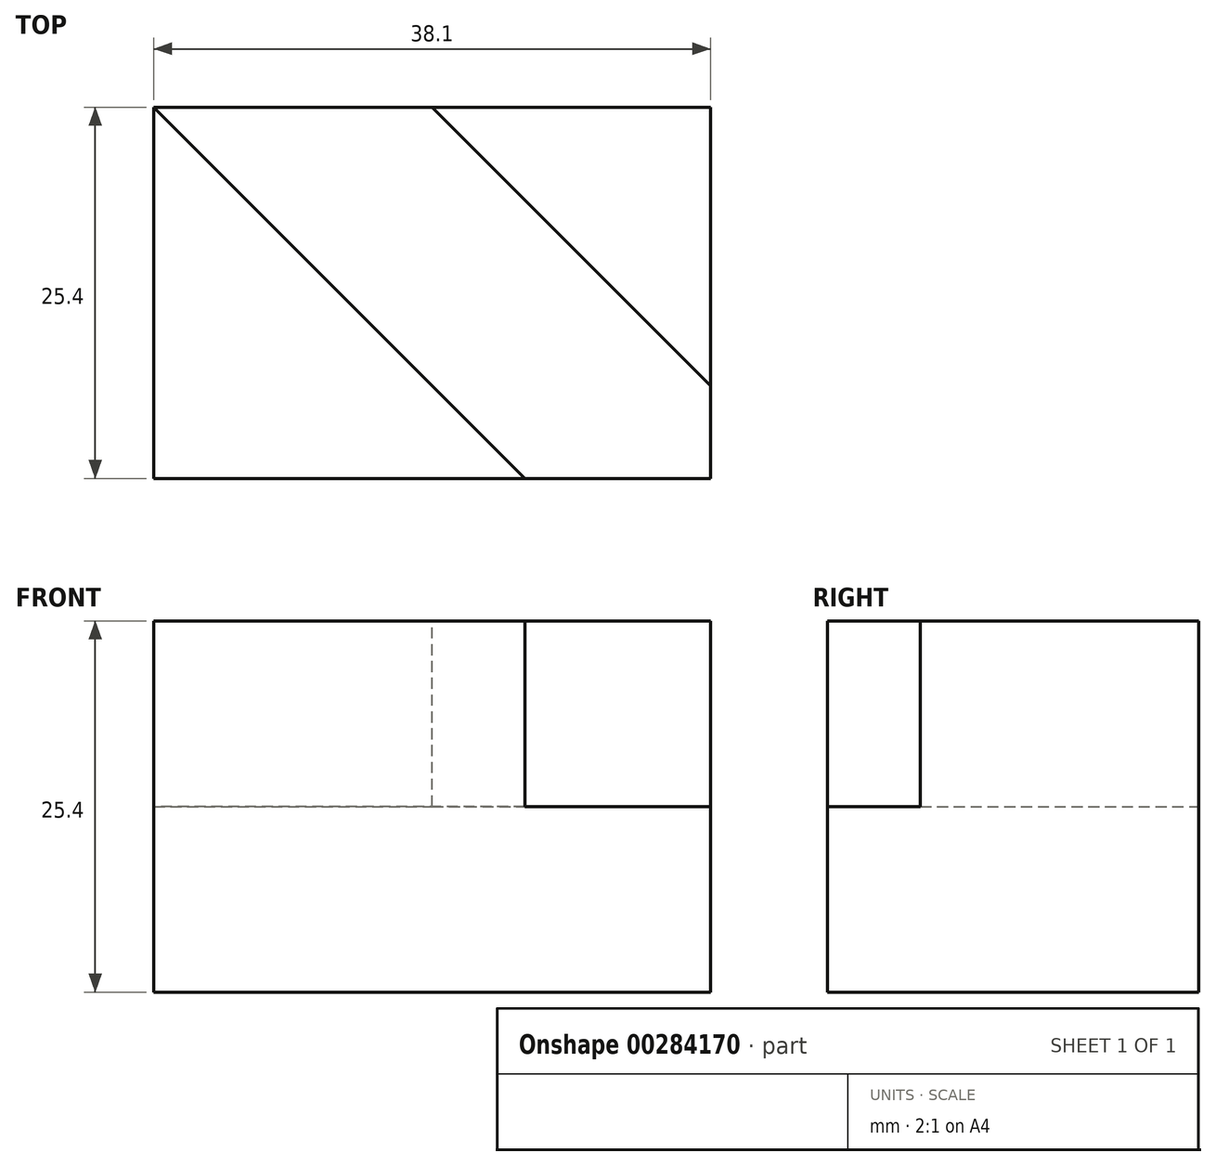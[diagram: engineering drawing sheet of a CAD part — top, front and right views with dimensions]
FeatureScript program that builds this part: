
annotation { "Feature Type Name" : "Feature", "Feature Type Description" : "" }
export const myFeature = defineFeature(function(context is Context, id is Id, definition is map)
    precondition{}
    {
        {
            var Q0;
            Q0=qCreatedBy(makeId("Front.planeOp"),FACE);
            var sketch = newSketch(context, id + "F0", { "sketchPlane" : qUnion([Q0])});
            skLineSegment(sketch, "E0.bottom", {"start": v(0, -25.4) * mm, "end": v(38.1, -25.4) * mm});
            skLineSegment(sketch, "E0.top", {"start": v(0, 0) * mm, "end": v(38.1, 0) * mm});
            skLineSegment(sketch, "E0.left", {"start": v(0, -25.4) * mm, "end": v(0, 0) * mm});
            skLineSegment(sketch, "E0.right", {"start": v(38.1, -25.4) * mm, "end": v(38.1, 0) * mm});
            skSolve(sketch);
        }
        {
            var Q0;
            Q0=makeQuery(id+"F0.imprint","IMPRINT",FACE,{"disambiguationData":[TD([[makeQuery(id+"F0.imprint","IMPRINT",EDGE,{"derivedFrom":sQuery(id+"F0.wireOp",EDGE,"E0.bottom")}),1.0]])]});
            extrude(context, id + "F1", {"entities" : qUnion([Q0]), "oppositeDirection" : true, "depth" : 25.4 * mm});
        }
        {
            var Q0;
            Q0=qCreatedBy(makeId("Top.planeOp"),FACE);
            var sketch = newSketch(context, id + "F2", { "sketchPlane" : qUnion([Q0])});
            skLineSegment(sketch, "E1", {"start": v(25.4, 0) * mm, "end": v(0, 25.4) * mm});
            skLineSegment(sketch, "E2", {"start": v(0, 25.4) * mm, "end": v(19.05, 25.4) * mm});
            skLineSegment(sketch, "E3", {"start": v(19.05, 25.4) * mm, "end": v(38.1, 6.35) * mm});
            skLineSegment(sketch, "E4", {"start": v(38.1, 6.35) * mm, "end": v(38.1, 0) * mm});
            skLineSegment(sketch, "E5", {"start": v(38.1, 0) * mm, "end": v(25.4, 0) * mm});
            skSolve(sketch);
        }
        {
            var Q0;
            Q0 = qSketchRegion(id + "F2", true);
            extrude(context, id + "F3", {"entities" : qUnion([Q0]), "operationType" : NewBodyOperationType.REMOVE, "oppositeDirection" : true, "depth" : 12.7 * mm});
        }
    });
